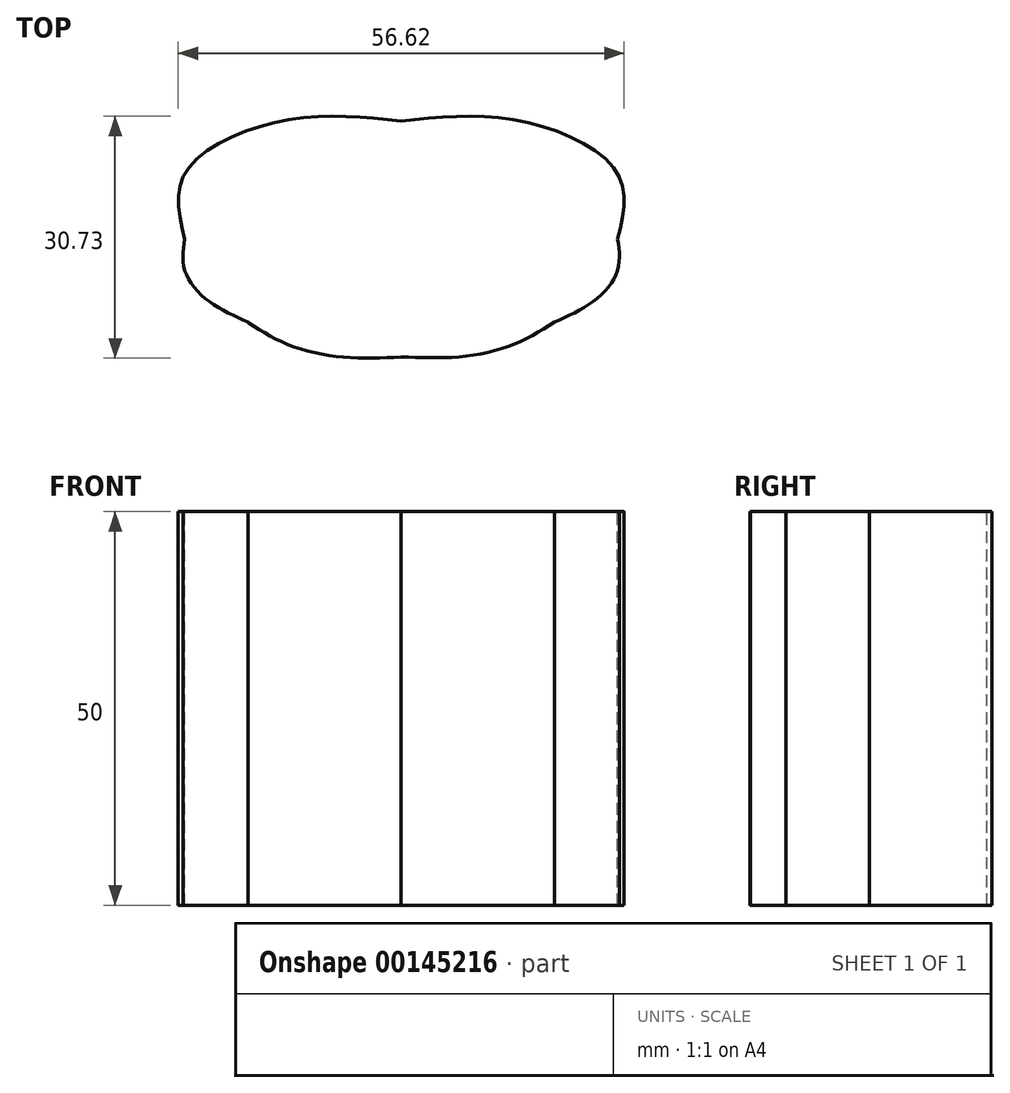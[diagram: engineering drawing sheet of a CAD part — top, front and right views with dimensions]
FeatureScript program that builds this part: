
annotation { "Feature Type Name" : "Feature", "Feature Type Description" : "" }
export const myFeature = defineFeature(function(context is Context, id is Id, definition is map)
    precondition{}
    {
        {
            var Q0;
            Q0=qCreatedBy(makeId("Top.planeOp"),FACE);
            var sketch = newSketch(context, id + "F0", { "sketchPlane" : qUnion([Q0])});
            skFitSpline(sketch, "E0", {"points": [v(-907.9, 1663.82) * mm, v(-907.9, 1659.85) * mm, v(-910.79, 1656.04) * mm, v(-915.94, 1653.23) * mm]});
            skFitSpline(sketch, "E1", {"points": [v(-915.94, 1653.23) * mm, v(-921.1, 1650.42) * mm, v(-928.1, 1648.84) * mm, v(-935.4, 1648.84) * mm]});
            skFitSpline(sketch, "E2", {"points": [v(-935.4, 1648.8) * mm, v(-942.68, 1648.8) * mm, v(-949.68, 1650.37) * mm, v(-954.84, 1653.18) * mm]});
            skFitSpline(sketch, "E3", {"points": [v(-954.84, 1653.23) * mm, v(-960, 1656.04) * mm, v(-962.9, 1659.85) * mm, v(-962.9, 1663.82) * mm]});
            skFitSpline(sketch, "E4", {"points": [v(-962.9, 1663.82) * mm, v(-962.9, 1672.09) * mm, v(-950.58, 1678.8) * mm, v(-935.4, 1678.8) * mm]});
            skFitSpline(sketch, "E5", {"points": [v(-935.4, 1678.8) * mm, v(-920.2, 1678.8) * mm, v(-907.9, 1672.09) * mm, v(-907.9, 1663.82) * mm]});
            skSolve(sketch);
        }
        {
            var Q0;
            Q0=sQuery(id+"F0.wireOp",EDGE,"E1");
            var Q1;
            Q1=sQuery(id+"F0.wireOp",EDGE,"E2");
            var Q2;
            Q2=sQuery(id+"F0.wireOp",EDGE,"E0");
            var Q3;
            Q3=sQuery(id+"F0.wireOp",EDGE,"E3");
            var Q4;
            Q4=sQuery(id+"F0.wireOp",EDGE,"E4");
            var Q5;
            Q5=sQuery(id+"F0.wireOp",EDGE,"E5");
            extrude(context, id + "F1", {"bodyType" : ToolBodyType.SURFACE, "surfaceEntities" : qUnion([Q0, Q1, Q2, Q3, Q4, Q5]), "depth" : 50 * mm});
        }
    });
